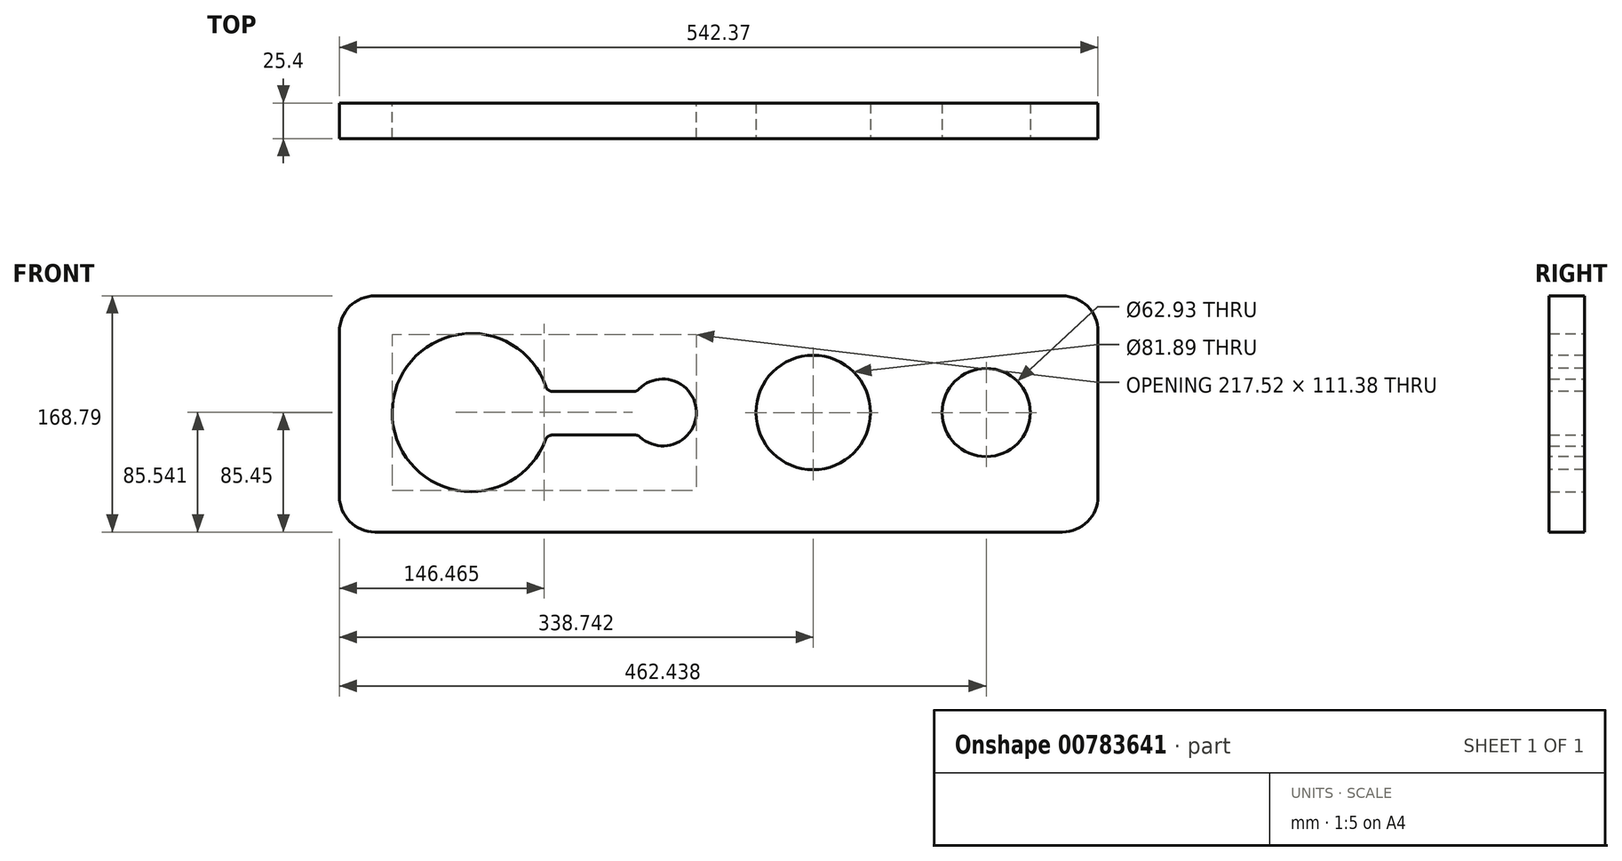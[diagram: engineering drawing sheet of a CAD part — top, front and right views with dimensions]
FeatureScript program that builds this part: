
annotation { "Feature Type Name" : "Feature", "Feature Type Description" : "" }
export const myFeature = defineFeature(function(context is Context, id is Id, definition is map)
    precondition{}
    {
        {
            var Q0;
            Q0=qCreatedBy(makeId("Front.planeOp"),FACE);
            var sketch = newSketch(context, id + "F0", { "sketchPlane" : qUnion([Q0])});
            skCircle(sketch, "E0", {"center": v(0, 0) * mm, "radius": 56.52 * mm});
            skCircle(sketch, "E1", {"center": v(137.1, 0) * mm, "radius": 23.92 * mm});
            skLineSegment(sketch, "E2.bottom", {"start": v(-94.22, 83.34) * mm, "end": v(448.15, 83.34) * mm});
            skLineSegment(sketch, "E2.top", {"start": v(-94.22, -85.45) * mm, "end": v(448.15, -85.45) * mm});
            skLineSegment(sketch, "E2.left", {"start": v(-94.22, 83.34) * mm, "end": v(-94.22, -85.45) * mm});
            skLineSegment(sketch, "E2.right", {"start": v(448.15, 83.34) * mm, "end": v(448.15, -85.45) * mm});
            skLineSegment(sketch, "E3.bottom", {"start": v(28.63, 15.06) * mm, "end": v(138.82, 15.06) * mm});
            skLineSegment(sketch, "E3.top", {"start": v(28.63, -16.16) * mm, "end": v(138.82, -16.16) * mm});
            skLineSegment(sketch, "E3.left", {"start": v(28.63, 15.06) * mm, "end": v(28.63, -16.16) * mm});
            skLineSegment(sketch, "E3.right", {"start": v(138.82, 15.06) * mm, "end": v(138.82, -16.16) * mm});
            skSolve(sketch);
        }
        {
            var Q0;
            Q0=makeQuery(id+"F0.imprint","IMPRINT",FACE,{"disambiguationData":[TD([[makeQuery(id+"F0.imprint","IMPRINT",EDGE,{"derivedFrom":sQuery(id+"F0.wireOp",EDGE,"E2.bottom")}),-1.0]])]});
            extrude(context, id + "F1", {"entities" : qUnion([Q0]), "depth" : 25.4 * mm, "offsetDistance" : 25.4 * mm});
        }
        {
            var Q0;
            Q0=makeQuery(id+"F1.opExtrude","SWEPT_EDGE",EDGE,{"disambiguationData":[OSD([sQuery(id+"F0.wireOp",EDGE,"E2.bottom"),sQuery(id+"F0.wireOp",EDGE,"E2.right")])]});
            var Q1;
            Q1=makeQuery(id+"F1.opExtrude","SWEPT_EDGE",EDGE,{"disambiguationData":[OSD([sQuery(id+"F0.wireOp",EDGE,"E2.top"),sQuery(id+"F0.wireOp",EDGE,"E2.right")])]});
            var Q2;
            Q2=makeQuery(id+"F1.opExtrude","SWEPT_EDGE",EDGE,{"disambiguationData":[OSD([sQuery(id+"F0.wireOp",EDGE,"E2.bottom"),sQuery(id+"F0.wireOp",EDGE,"E2.left")])]});
            var Q3;
            Q3=makeQuery(id+"F1.opExtrude","SWEPT_EDGE",EDGE,{"disambiguationData":[OSD([sQuery(id+"F0.wireOp",EDGE,"E2.top"),sQuery(id+"F0.wireOp",EDGE,"E2.left")])]});
            fillet(context, id + "F2", {"entities" : qUnion([Q0, Q1, Q2, Q3]), "radius" : 25.4 * mm, "tangentPropagation" : true, "allowEdgeOverflow" : false});
        }
        {
            var Q0;
            Q0=makeQuery(id+"F1.opExtrude","SWEPT_EDGE",EDGE,{"disambiguationData":[OSD([sQuery(id+"F0.wireOp",EDGE,"E0"),sQuery(id+"F0.wireOp",EDGE,"E3.bottom")])]});
            var Q1;
            Q1=makeQuery(id+"F1.opExtrude","SWEPT_EDGE",EDGE,{"disambiguationData":[OSD([sQuery(id+"F0.wireOp",EDGE,"E1"),sQuery(id+"F0.wireOp",EDGE,"E3.top")])]});
            var Q2;
            Q2=makeQuery(id+"F1.opExtrude","SWEPT_EDGE",EDGE,{"disambiguationData":[OSD([sQuery(id+"F0.wireOp",EDGE,"E0"),sQuery(id+"F0.wireOp",EDGE,"E3.top")])]});
            var Q3;
            Q3=makeQuery(id+"F1.opExtrude","SWEPT_EDGE",EDGE,{"disambiguationData":[OSD([sQuery(id+"F0.wireOp",EDGE,"E1"),sQuery(id+"F0.wireOp",EDGE,"E3.bottom")])]});
            fillet(context, id + "F3", {"entities" : qUnion([Q0, Q1, Q2, Q3]), "radius" : 5.08 * mm, "tangentPropagation" : true, "allowEdgeOverflow" : false});
        }
        {
            var Q0;
            Q0=makeQuery(id+"F1.opExtrude","CAP_FACE",FACE,{"disambiguationData":[OSD([sQuery(id+"F0.wireOp",EDGE,"E0"),sQuery(id+"F0.wireOp",EDGE,"E1"),sQuery(id+"F0.wireOp",EDGE,"E2.bottom"),sQuery(id+"F0.wireOp",EDGE,"E2.top"),sQuery(id+"F0.wireOp",EDGE,"E2.left"),sQuery(id+"F0.wireOp",EDGE,"E2.right"),sQuery(id+"F0.wireOp",EDGE,"E3.bottom"),sQuery(id+"F0.wireOp",EDGE,"E3.top")])],"isStart":false});
            var sketch = newSketch(context, id + "F4", { "sketchPlane" : qUnion([Q0])});
            skCircle(sketch, "E4", {"center": v(244.52, 0) * mm, "radius": 40.95 * mm});
            skCircle(sketch, "E5", {"center": v(368.22, 0) * mm, "radius": 31.47 * mm});
            skSolve(sketch);
        }
        {
            var Q0;
            Q0=makeQuery(id+"F4.imprint","IMPRINT",FACE,{"disambiguationData":[TD([[makeQuery(id+"F4.imprint","IMPRINT",EDGE,{"derivedFrom":sQuery(id+"F4.wireOp",EDGE,"E4")}),1.0]])]});
            var Q1;
            Q1=makeQuery(id+"F4.imprint","IMPRINT",FACE,{"disambiguationData":[TD([[makeQuery(id+"F4.imprint","IMPRINT",EDGE,{"derivedFrom":sQuery(id+"F4.wireOp",EDGE,"E5")}),1.0]])]});
            extrude(context, id + "F5", {"entities" : qUnion([Q0, Q1]), "operationType" : NewBodyOperationType.REMOVE, "oppositeDirection" : true, "depth" : 25.4 * mm, "offsetDistance" : 25.4 * mm});
        }
    });
